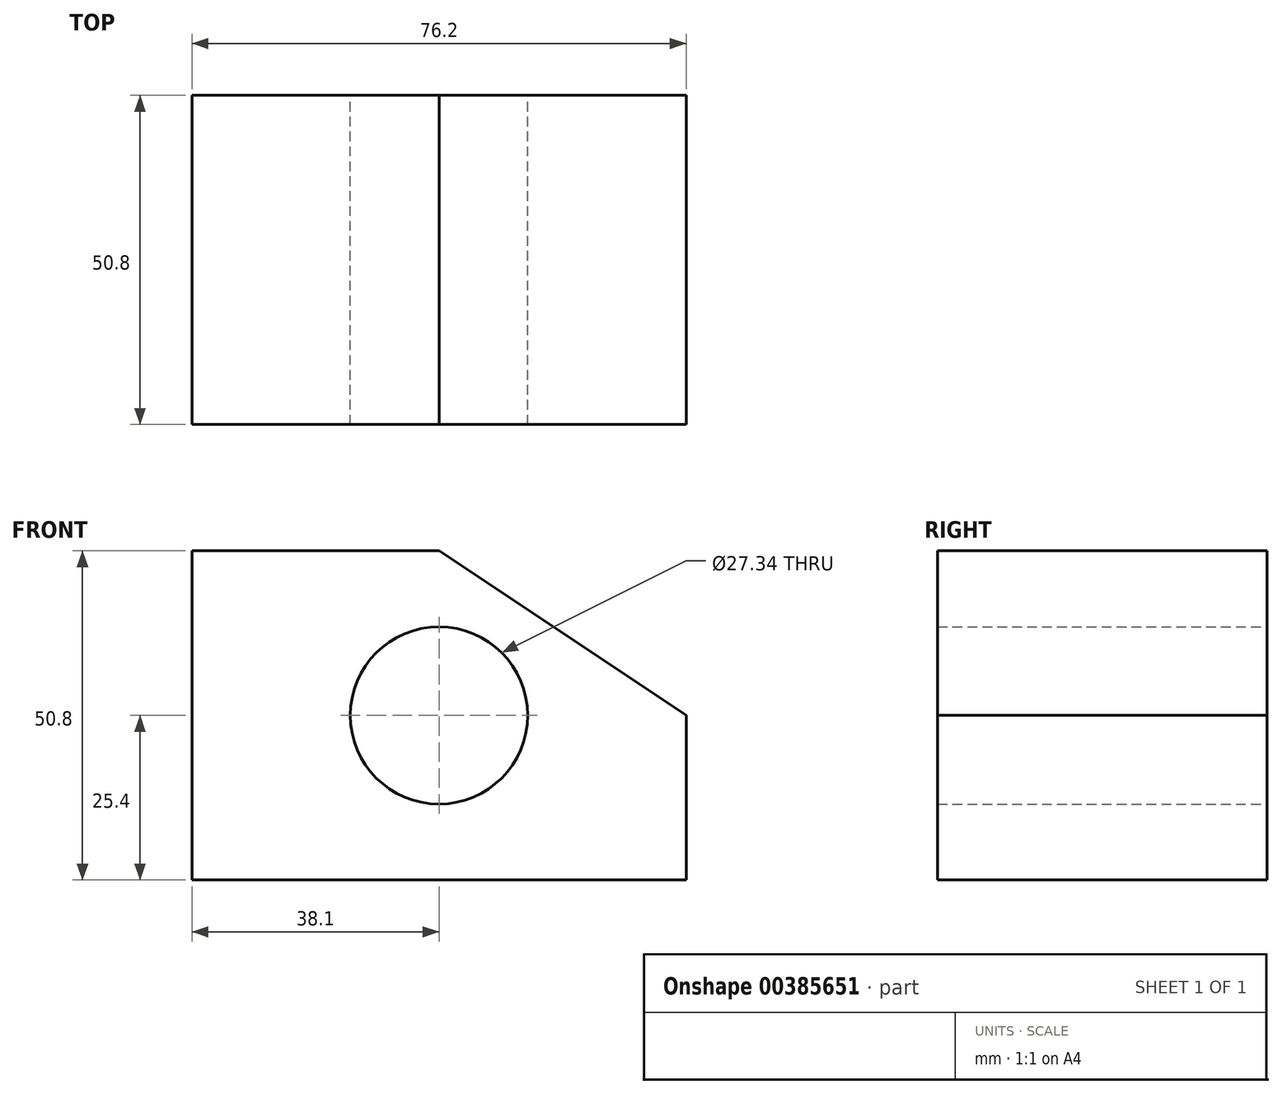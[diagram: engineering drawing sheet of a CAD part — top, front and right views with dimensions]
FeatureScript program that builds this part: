
annotation { "Feature Type Name" : "Feature", "Feature Type Description" : "" }
export const myFeature = defineFeature(function(context is Context, id is Id, definition is map)
    precondition{}
    {
        {
            var Q0;
            Q0=qCreatedBy(makeId("Front.planeOp"),FACE);
            var sketch = newSketch(context, id + "F0", { "sketchPlane" : qUnion([Q0])});
            skLineSegment(sketch, "E0", {"start": v(-38.1, -25.4) * mm, "end": v(38.1, -25.4) * mm});
            skLineSegment(sketch, "E1", {"start": v(-38.1, -25.4) * mm, "end": v(-38.1, 25.4) * mm});
            skLineSegment(sketch, "E2", {"start": v(-38.1, 25.4) * mm, "end": v(0, 25.4) * mm});
            skLineSegment(sketch, "E3", {"start": v(38.1, -25.4) * mm, "end": v(38.1, 0) * mm});
            skLineSegment(sketch, "E4", {"start": v(38.1, 0) * mm, "end": v(0, 25.4) * mm});
            skCircle(sketch, "E5", {"center": v(0, 0) * mm, "radius": 13.67 * mm});
            skSolve(sketch);
        }
        {
            var Q0;
            Q0=makeQuery(id+"F0.imprint","IMPRINT",FACE,{"disambiguationData":[TD([[makeQuery(id+"F0.imprint","IMPRINT",EDGE,{"derivedFrom":sQuery(id+"F0.wireOp",EDGE,"E0")}),1.0]])]});
            extrude(context, id + "F1", {"entities" : qUnion([Q0]), "depth" : 50.8 * mm});
        }
    });
